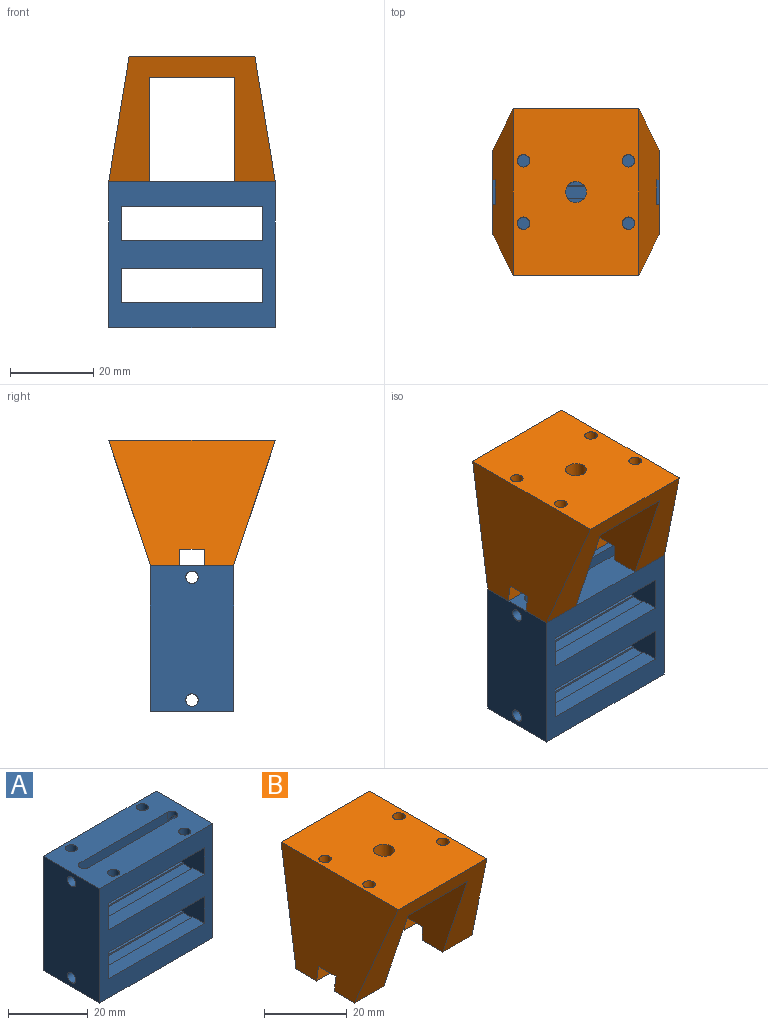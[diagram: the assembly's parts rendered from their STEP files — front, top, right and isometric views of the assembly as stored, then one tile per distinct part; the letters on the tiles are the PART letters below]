
ASSEMBLY  parts=2 mates=1
PART A: 88 faces, bbox 40x20x35 mm
  f0: plane 34x0.4mm, normal (0,-1,0), area 13.6mm2, adj f24,f67,f69,f71
  f1: plane 34x0.4mm, normal (0,-1,0), area 13.6mm2, adj f41,f67,f69,f70
  f2: plane 34x0.4mm, normal (0,1,0), area 13.6mm2, adj f32,f66,f67,f69
  f3: plane 34x0.4mm, normal (0,1,0), area 13.6mm2, adj f33,f67,f68,f69
  f4: plane 1.5x1.5mm, normal (0,0,1), area 0.5mm2, adj f38,f67,f75
  f5: plane 1.5x1.5mm, normal (0,0,-1), area 0.5mm2, adj f45,f64,f73
  f6: plane 34x0.4mm, normal (0,1,0), area 13.6mm2, adj f50,f62,f64,f65
  f7: plane 34x0.4mm, normal (0,1,0), area 13.6mm2, adj f51,f62,f63,f64
  f8: plane 34x0.4mm, normal (0,-1,0), area 13.6mm2, adj f42,f60,f62,f64
  f9: plane 34x0.4mm, normal (0,-1,0), area 13.6mm2, adj f59,f61,f62,f64
  f10: plane 1.5x1.5mm, normal (0,0,1), area 0.5mm2, adj f14,f36,f69
  f11: plane 1.5x1.5mm, normal (0,0,-1), area 0.5mm2, adj f12,f47,f62
  f12: cylinder r=1.5mm len=3mm, axis (0,0,1), area 8.5mm2, adj f11,f18,f45,f47,f87
  f13: cylinder r=1.5mm len=3mm, axis (0,0,1), area 8.5mm2, adj f16,f45,f47,f86
  f14: cylinder r=1.5mm len=3mm, axis (0,0,-1), area 8.5mm2, adj f10,f17,f36,f38,f85
  f15: cylinder r=1.5mm len=3mm, axis (0,0,-1), area 8.5mm2, adj f23,f36,f38,f84
  f16: plane 40x20mm, normal (0,0,1), area 671.7mm2, adj f13,f19,f20,f21,f22,f45,f47,f72
  f17: plane 1.5x1.5mm, normal (0,0,1), area 0.5mm2, adj f14,f38,f69
  f18: plane 1.5x1.5mm, normal (0,0,-1), area 0.5mm2, adj f12,f45,f62
  f19: plane 35x20mm, normal (-1,0,0), area 685.9mm2, adj f16,f21,f22,f23,f84,f86
  f20: plane 35x20mm, normal (1,0,0), area 685.9mm2, adj f16,f21,f22,f23,f85,f87
  f21: plane 40x35mm, normal (0,-1,0), area 842.4mm2, adj f16,f19,f20,f23,f62,f63,f64,f65
  f22: plane 40x35mm, normal (0,1,0), area 842.4mm2, adj f16,f19,f20,f23,f60,f61,f62,f64
  f23: plane 40x20mm, normal (0,0,-1), area 699.9mm2, adj f15,f19,f20,f21,f22,f36,f38,f74
  f24: plane 34x3.5mm, normal (0,0,-1), area 119mm2, adj f0,f25,f67,f69
  f25: plane 34x0.4mm, normal (0,1,0), area 13.6mm2, adj f24,f26,f67,f69
  f26: plane 34x1mm, normal (0,0,-1), area 34mm2, adj f25,f27,f67,f69
  f27: plane 34x0.4mm, normal (0,-1,0), area 13.6mm2, adj f26,f28,f67,f69
  f28: plane 34x3mm, normal (0,0,-1), area 102mm2, adj f27,f29,f67,f69
  f29: plane 34x0.4mm, normal (0,1,0), area 13.6mm2, adj f28,f30,f67,f69
  f30: plane 34x1mm, normal (0,0,-1), area 34mm2, adj f29,f31,f67,f69
  f31: plane 34x0.4mm, normal (0,-1,0), area 13.6mm2, adj f30,f32,f67,f69
  f32: plane 34x3.5mm, normal (0,0,-1), area 119mm2, adj f2,f31,f67,f69
  f33: plane 34x3.5mm, normal (0,0,1), area 119mm2, adj f3,f34,f67,f69
  f34: plane 34x0.4mm, normal (0,-1,0), area 13.6mm2, adj f33,f35,f67,f69
  f35: plane 34x1mm, normal (0,0,1), area 34mm2, adj f34,f36,f67,f69
  f36: plane 34x5.9mm, normal (0,1,0), area 184.1mm2, adj f10,f14,f15,f23,f35,f37,f67,f69
  f37: plane 1.5x1.5mm, normal (0,0,1), area 0.5mm2, adj f36,f67,f75
  f38: plane 34x5.9mm, normal (0,-1,0), area 184.1mm2, adj f4,f14,f15,f17,f23,f39,f67,f69
  f39: plane 34x1mm, normal (0,0,1), area 34mm2, adj f38,f40,f67,f69
  f40: plane 34x0.4mm, normal (0,1,0), area 13.6mm2, adj f39,f41,f67,f69
  f41: plane 34x3.5mm, normal (0,0,1), area 119mm2, adj f1,f40,f67,f69
  f42: plane 34x3.5mm, normal (0,0,-1), area 119mm2, adj f8,f43,f62,f64
  f43: plane 34x0.4mm, normal (0,1,0), area 13.6mm2, adj f42,f44,f62,f64
  f44: plane 34x1mm, normal (0,0,-1), area 34mm2, adj f43,f45,f62,f64
  f45: plane 34x5.9mm, normal (0,-1,0), area 184.1mm2, adj f5,f12,f13,f16,f18,f44,f62,f64
  f46: plane 1.5x1.5mm, normal (0,0,-1), area 0.5mm2, adj f47,f64,f73
  f47: plane 34x5.9mm, normal (0,1,0), area 184.1mm2, adj f11,f12,f13,f16,f46,f48,f62,f64
  f48: plane 34x1mm, normal (0,0,-1), area 34mm2, adj f47,f49,f62,f64
  f49: plane 34x0.4mm, normal (0,-1,0), area 13.6mm2, adj f48,f50,f62,f64
  f50: plane 34x3.5mm, normal (0,0,-1), area 119mm2, adj f6,f49,f62,f64
  f51: plane 34x3.5mm, normal (0,0,1), area 119mm2, adj f7,f52,f62,f64
  f52: plane 34x0.4mm, normal (0,-1,0), area 13.6mm2, adj f51,f53,f62,f64
  f53: plane 34x1mm, normal (0,0,1), area 34mm2, adj f52,f54,f62,f64
  f54: plane 34x0.4mm, normal (0,1,0), area 13.6mm2, adj f53,f55,f62,f64
  f55: plane 34x3mm, normal (0,0,1), area 102mm2, adj f54,f56,f62,f64
  f56: plane 34x0.4mm, normal (0,-1,0), area 13.6mm2, adj f55,f57,f62,f64
  f57: plane 34x1mm, normal (0,0,1), area 34mm2, adj f56,f58,f62,f64
  f58: plane 34x0.4mm, normal (0,1,0), area 13.6mm2, adj f57,f59,f62,f64
  f59: plane 34x3.5mm, normal (0,0,1), area 119mm2, adj f9,f58,f62,f64
  f60: plane 34x4mm, normal (0,0,-1), area 136mm2, adj f8,f22,f62,f64
  f61: plane 34x4mm, normal (0,0,1), area 136mm2, adj f9,f22,f62,f64
  f62: plane 20x9mm, normal (-1,0,0), area 172mm2, adj f6,f7,f8,f9,f11,f18,f21,f22
  f63: plane 34x4mm, normal (0,0,1), area 136mm2, adj f7,f21,f62,f64
  f64: plane 20x9mm, normal (1,0,0), area 172mm2, adj f5,f6,f7,f8,f9,f21,f22,f42
  f65: plane 34x4mm, normal (0,0,-1), area 136mm2, adj f6,f21,f62,f64
  f66: plane 34x4mm, normal (0,0,-1), area 136mm2, adj f2,f21,f67,f69
  f67: plane 20x9mm, normal (1,0,0), area 172mm2, adj f0,f1,f2,f3,f4,f21,f22,f24
  f68: plane 34x4mm, normal (0,0,1), area 136mm2, adj f3,f21,f67,f69
  f69: plane 20x9mm, normal (-1,0,0), area 172mm2, adj f0,f1,f2,f3,f10,f17,f21,f22
  f70: plane 34x4mm, normal (0,0,1), area 136mm2, adj f1,f22,f67,f69
  f71: plane 34x4mm, normal (0,0,-1), area 136mm2, adj f0,f22,f67,f69
  f72: cylinder r=1.5mm len=3mm, axis (0,0,1), area 8.5mm2, adj f16,f45,f47,f87
  f73: cylinder r=1.5mm len=3mm, axis (0,0,1), area 8.5mm2, adj f5,f45,f46,f47,f86
  f74: cylinder r=1.5mm len=3mm, axis (0,0,-1), area 8.5mm2, adj f23,f36,f38,f85
  f75: cylinder r=1.5mm len=3mm, axis (0,0,-1), area 8.5mm2, adj f4,f36,f37,f38,f84
  f76: cylinder r=1.5mm len=5mm, axis (0,0,1), area 47.1mm2, adj f16,f77
  f77: plane 3x3mm, normal (0,0,1), area 7.1mm2, adj f76
  f78: cylinder r=1.5mm len=5mm, axis (0,0,1), area 47.1mm2, adj f16,f79
  f79: plane 3x3mm, normal (0,0,1), area 7.1mm2, adj f78
  f80: cylinder r=1.5mm len=5mm, axis (0,0,1), area 47.1mm2, adj f16,f81
  f81: plane 3x3mm, normal (0,0,1), area 7.1mm2, adj f80
  f82: cylinder r=1.5mm len=5mm, axis (0,0,1), area 47.1mm2, adj f16,f83
  f83: plane 3x3mm, normal (0,0,1), area 7.1mm2, adj f82
  f84: cylinder r=1.5mm len=4.5mm, axis (1,0,0), area 33.4mm2, adj f15,f19,f75
  f85: cylinder r=1.5mm len=4.5mm, axis (1,0,0), area 33.4mm2, adj f14,f20,f74
  f86: cylinder r=1.5mm len=4.5mm, axis (1,0,0), area 33.4mm2, adj f13,f19,f73
  f87: cylinder r=1.5mm len=4.5mm, axis (1,0,0), area 33.4mm2, adj f12,f20,f72
PART B: 23 faces, bbox 40x40x30.1 mm
  f0: plane 9.9x7mm, normal (0,0,-1), area 62.2mm2, adj f4,f8,f14,f16,f19
  f1: plane 9.9x7mm, normal (0,0,-1), area 62.2mm2, adj f4,f8,f13,f17,f18
  f2: plane 9.9x7mm, normal (0,0,-1), area 62.2mm2, adj f6,f7,f10,f18,f20
  f3: plane 9.9x7mm, normal (0,0,-1), area 62.2mm2, adj f6,f7,f11,f19,f21
  f4: plane 36.68x25.1mm, normal (1,0,0), area 687.3mm2, adj f0,f1,f5,f15,f16,f17,f18,f19
  f5: plane 36.68x20.2mm, normal (0,0,-1), area 721.3mm2, adj f4,f6,f12,f18,f19
  f6: plane 36.68x25.1mm, normal (-1,0,0), area 687.3mm2, adj f2,f3,f5,f18,f19,f20,f21,f22
  f7: plane 40x30.1mm, normal (0.99,0,0.16), area 890.6mm2, adj f2,f3,f9,f18,f19,f20,f21,f22
  f8: plane 40x30.1mm, normal (-0.99,0,0.16), area 890.6mm2, adj f0,f1,f9,f15,f16,f17,f18,f19
  f9: plane 40x30.2mm, normal (0,0,1), area 1160.1mm2, adj f7,f8,f10,f11,f12,f13,f14,f18
  f10: cylinder r=1.5mm len=30.1mm, axis (0,0,1), area 283.7mm2, adj f2,f9
  f11: cylinder r=1.5mm len=30.1mm, axis (0,0,1), area 283.7mm2, adj f3,f9
  f12: cylinder r=2.5mm len=5mm, axis (0,0,1), area 78.5mm2, adj f5,f9
  f13: cylinder r=1.5mm len=30.1mm, axis (0,0,1), area 283.7mm2, adj f1,f9
  f14: cylinder r=1.5mm len=30.1mm, axis (0,0,1), area 283.7mm2, adj f0,f9
  f15: plane 9.25x6mm, normal (0,0,-1), area 55.5mm2, adj f4,f8,f16,f17
  f16: plane 9.9x4mm, normal (0,1,0), area 38.3mm2, adj f0,f4,f8,f15
  f17: plane 9.9x4mm, normal (0,-1,0), area 38.3mm2, adj f1,f4,f8,f15
  f18: plane 40x30.1mm, normal (0,0.95,-0.32), area 579mm2, adj f1,f2,f4,f5,f6,f7,f8,f9
  f19: plane 40x30.1mm, normal (0,-0.95,-0.32), area 579mm2, adj f0,f3,f4,f5,f6,f7,f8,f9
  f20: plane 9.9x4mm, normal (0,-1,0), area 38.3mm2, adj f2,f6,f7,f22
  f21: plane 9.9x4mm, normal (0,1,0), area 38.3mm2, adj f3,f6,f7,f22
  f22: plane 9.25x6mm, normal (0,0,-1), area 55.5mm2, adj f6,f7,f20,f21
PLACE A at identity
PLACE B t=(0,20,60.1)mm
MATE parallel B.f14 <-> A.f82  axis (0,0,-1) through (-12.6,-7.5,35)mm
